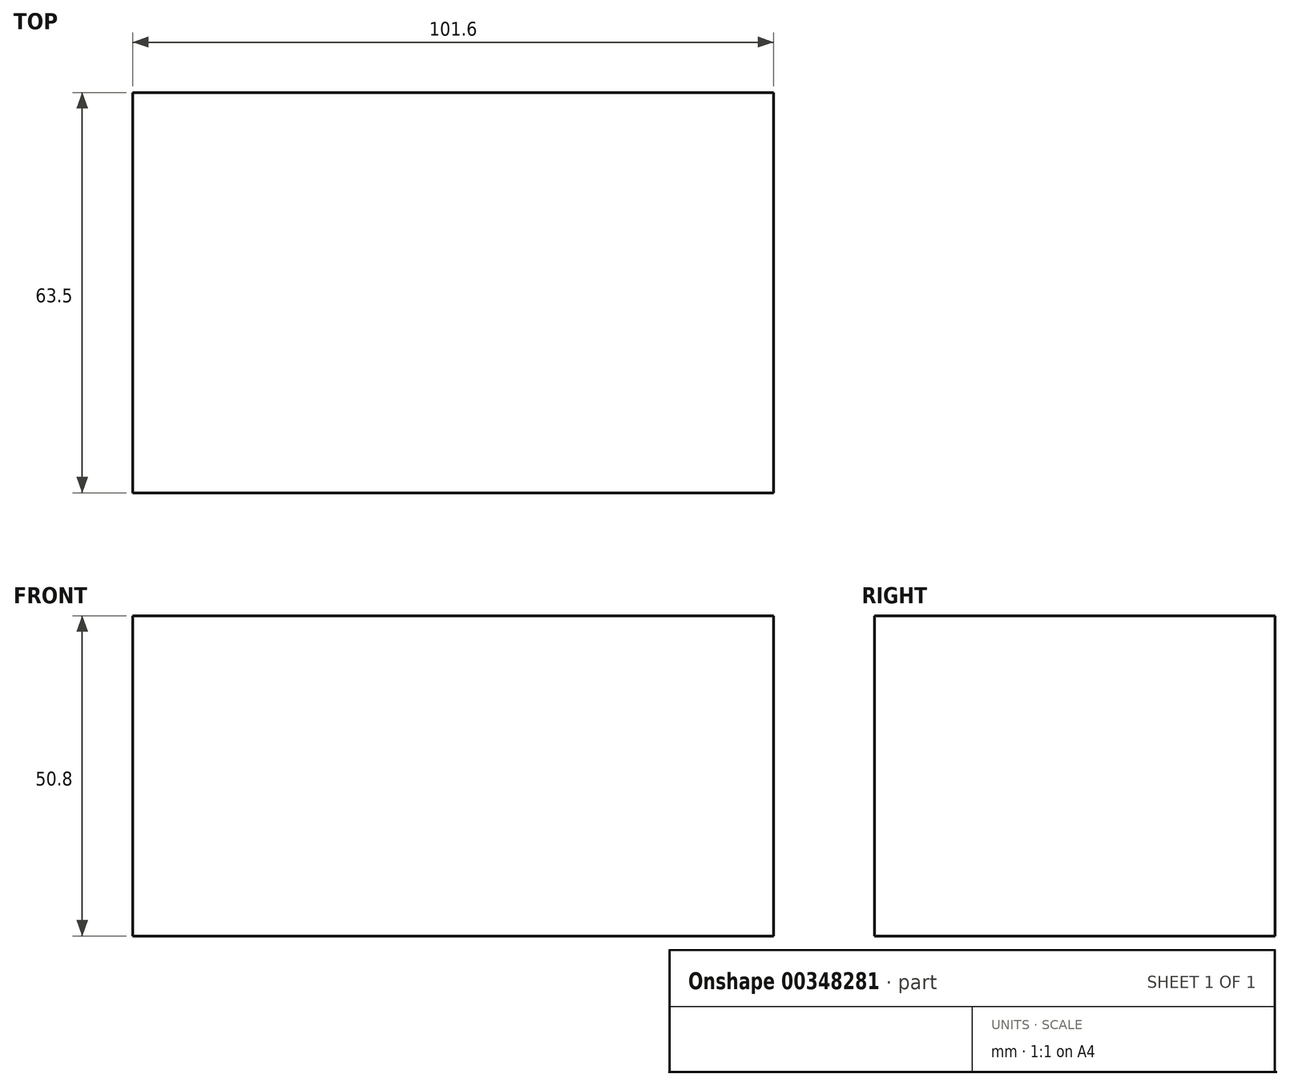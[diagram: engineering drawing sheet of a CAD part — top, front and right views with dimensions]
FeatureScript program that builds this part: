
annotation { "Feature Type Name" : "Feature", "Feature Type Description" : "" }
export const myFeature = defineFeature(function(context is Context, id is Id, definition is map)
    precondition{}
    {
        {
            var Q0;
            Q0=qCreatedBy(makeId("Front.planeOp"),FACE);
            var sketch = newSketch(context, id + "F0", { "sketchPlane" : qUnion([Q0])});
            skLineSegment(sketch, "E0.bottom", {"start": v(50.8, 25.4) * mm, "end": v(-50.8, 25.4) * mm});
            skLineSegment(sketch, "E0.top", {"start": v(50.8, -25.4) * mm, "end": v(-50.8, -25.4) * mm});
            skLineSegment(sketch, "E0.left", {"start": v(50.8, 25.4) * mm, "end": v(50.8, -25.4) * mm});
            skLineSegment(sketch, "E0.right", {"start": v(-50.8, 25.4) * mm, "end": v(-50.8, -25.4) * mm});
            skPoint(sketch, "E0.middle", {"position": v(0, 0) * mm});
            skSolve(sketch);
        }
        {
            var Q0;
            Q0=makeQuery(id+"F0.imprint","IMPRINT",FACE,{"disambiguationData":[TD([[makeQuery(id+"F0.imprint","IMPRINT",EDGE,{"derivedFrom":sQuery(id+"F0.wireOp",EDGE,"E0.bottom")}),1.0]])]});
            extrude(context, id + "F1", {"entities" : qUnion([Q0]), "depth" : 63.5 * mm});
        }
    });
